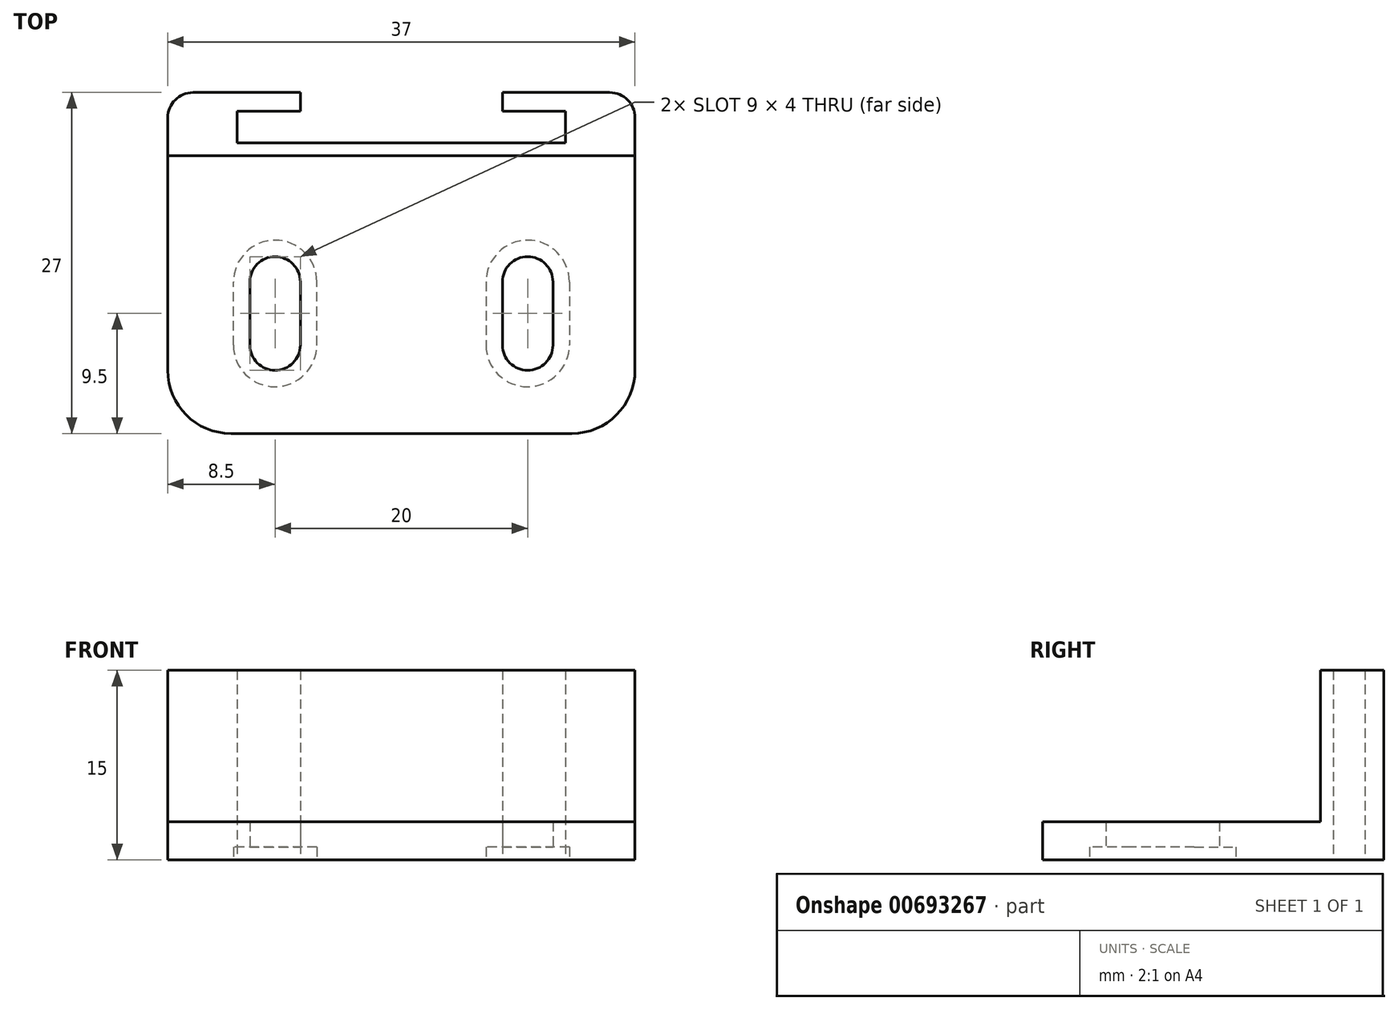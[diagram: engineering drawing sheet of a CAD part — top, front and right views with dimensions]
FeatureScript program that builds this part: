
annotation { "Feature Type Name" : "Feature", "Feature Type Description" : "" }
export const myFeature = defineFeature(function(context is Context, id is Id, definition is map)
    precondition{}
    {
        {
            var Q0;
            Q0=qCreatedBy(makeId("Top.planeOp"),FACE);
            var sketch = newSketch(context, id + "F0", { "sketchPlane" : qUnion([Q0])});
            skLineSegment(sketch, "E0.bottom", {"start": v(0, 0) * mm, "end": v(32, 0) * mm});
            skLineSegment(sketch, "E0.top", {"start": v(0, 22) * mm, "end": v(32, 22) * mm});
            skLineSegment(sketch, "E0.left", {"start": v(0, 0) * mm, "end": v(0, 22) * mm});
            skLineSegment(sketch, "E0.right", {"start": v(32, 0) * mm, "end": v(32, 22) * mm});
            skLineSegment(sketch, "E1.bottom", {"start": v(4, 5) * mm, "end": v(8, 5) * mm});
            skLineSegment(sketch, "E1.top", {"start": v(4, 14) * mm, "end": v(8, 14) * mm});
            skLineSegment(sketch, "E1.left", {"start": v(4, 5) * mm, "end": v(4, 14) * mm});
            skLineSegment(sketch, "E1.right", {"start": v(8, 5) * mm, "end": v(8, 14) * mm});
            skLineSegment(sketch, "E2.bottom", {"start": v(24, 14) * mm, "end": v(28, 14) * mm});
            skLineSegment(sketch, "E2.top", {"start": v(24, 5) * mm, "end": v(28, 5) * mm});
            skLineSegment(sketch, "E2.left", {"start": v(24, 14) * mm, "end": v(24, 5) * mm});
            skLineSegment(sketch, "E2.right", {"start": v(28, 14) * mm, "end": v(28, 5) * mm});
            skLineSegment(sketch, "E3", {"start": v(0, 22) * mm, "end": v(0, 23) * mm});
            skLineSegment(sketch, "E4", {"start": v(32, 22) * mm, "end": v(32, 23) * mm});
            skLineSegment(sketch, "E5", {"start": v(32, 23) * mm, "end": v(0, 23) * mm});
            skLineSegment(sketch, "E6", {"start": v(0, 23) * mm, "end": v(0, 27) * mm});
            skLineSegment(sketch, "E7", {"start": v(0, 27) * mm, "end": v(8, 27) * mm});
            skLineSegment(sketch, "E8", {"start": v(8, 27) * mm, "end": v(8, 25.5) * mm});
            skLineSegment(sketch, "E9", {"start": v(8, 25.5) * mm, "end": v(3, 25.5) * mm});
            skLineSegment(sketch, "E10", {"start": v(3, 25.5) * mm, "end": v(3, 23) * mm});
            skPoint(sketch, "E11", {"position": v(16, 23) * mm});
            skPoint(sketch, "E12", {"position": v(16, 0) * mm});
            skPoint(sketch, "E13", {"position": v(16, 22) * mm});
            skLineSegment(sketch, "E14", {"start": v(16, 23) * mm, "end": v(16, 0) * mm});
            skLineSegment(sketch, "E15.MirrorCS", {"start": v(32, 27) * mm, "end": v(24, 27) * mm});
            skLineSegment(sketch, "E16.MirrorCS", {"start": v(32, 23) * mm, "end": v(32, 27) * mm});
            skLineSegment(sketch, "E17.MirrorCS", {"start": v(29, 25.5) * mm, "end": v(29, 23) * mm});
            skLineSegment(sketch, "E18.MirrorCS", {"start": v(24, 25.5) * mm, "end": v(29, 25.5) * mm});
            skLineSegment(sketch, "E19.MirrorCS", {"start": v(24, 27) * mm, "end": v(24, 25.5) * mm});
            skSolve(sketch);
        }
        {
            var Q0;
            {var subQ0=sQuery(id+"F0.wireOp",EDGE,"E0.left");Q0=makeQuery(id+"F0.imprint","IMPRINT",FACE,{"disambiguationData":[TD([[makeQuery(id+"F0.imprint","IMPRINT",EDGE,{"derivedFrom":subQ0}),-1.0]])]});}
            var Q1;
            {var subQ0=sQuery(id+"F0.wireOp",EDGE,"E0.right");Q1=makeQuery(id+"F0.imprint","IMPRINT",FACE,{"disambiguationData":[TD([[makeQuery(id+"F0.imprint","IMPRINT",EDGE,{"derivedFrom":subQ0}),1.0]])]});}
            extrude(context, id + "F1", {"entities" : qUnion([Q0, Q1]), "depth" : 3 * mm, "offsetDistance" : 25 * mm});
        }
        {
            var Q0;
            {var subQ0=sQuery(id+"F0.wireOp",EDGE,"E6");Q0=makeQuery(id+"F0.imprint","IMPRINT",FACE,{"disambiguationData":[TD([[makeQuery(id+"F0.imprint","IMPRINT",EDGE,{"derivedFrom":subQ0}),-1.0]])]});}
            var Q1;
            {var subQ4=sQuery(id+"F0.wireOp",EDGE,"E3");Q1=makeQuery(id+"F0.imprint","IMPRINT",FACE,{"disambiguationData":[TD([[makeQuery(id+"F0.imprint","IMPRINT",EDGE,{"derivedFrom":subQ4}),-1.0]])]});}
            var Q2;
            {var subQ4=sQuery(id+"F0.wireOp",EDGE,"E4");Q2=makeQuery(id+"F0.imprint","IMPRINT",FACE,{"disambiguationData":[TD([[makeQuery(id+"F0.imprint","IMPRINT",EDGE,{"derivedFrom":subQ4}),1.0]])]});}
            var Q3;
            Q3=makeQuery(id+"F0.imprint","IMPRINT",FACE,{"disambiguationData":[TD([[makeQuery(id+"F0.imprint","IMPRINT",EDGE,{"derivedFrom":sQuery(id+"F0.wireOp",EDGE,"E15.MirrorCS")}),1.0]])]});
            extrude(context, id + "F2", {"entities" : qUnion([Q0, Q1, Q2, Q3]), "operationType" : NewBodyOperationType.ADD, "depth" : 15 * mm, "offsetDistance" : 25 * mm});
        }
        {
            var Q0;
            Q0=makeQuery(id+"F2.boolean.opBoolean","MERGE",FACE,{"derivedFrom":[makeQuery(id+"F1.opExtrude","SWEPT_FACE",FACE,{"disambiguationData":[OSD([sQuery(id+"F0.wireOp",EDGE,"E0.right")])]}),makeQuery(id+"F2.opExtrude","SWEPT_FACE",FACE,{"disambiguationData":[OSD([sQuery(id+"F0.wireOp",EDGE,"E4"),sQuery(id+"F0.wireOp",EDGE,"E16.MirrorCS")])]})]});
            extrude(context, id + "F3", {"entities" : qUnion([Q0]), "operationType" : NewBodyOperationType.ADD, "depth" : 2.5 * mm, "offsetDistance" : 25 * mm});
        }
        {
            var Q0;
            Q0=makeQuery(id+"F2.boolean.opBoolean","MERGE",FACE,{"derivedFrom":[makeQuery(id+"F1.opExtrude","SWEPT_FACE",FACE,{"disambiguationData":[OSD([sQuery(id+"F0.wireOp",EDGE,"E0.left")])]}),makeQuery(id+"F2.opExtrude","SWEPT_FACE",FACE,{"disambiguationData":[OSD([sQuery(id+"F0.wireOp",EDGE,"E3"),sQuery(id+"F0.wireOp",EDGE,"E6")])]})]});
            extrude(context, id + "F4", {"entities" : qUnion([Q0]), "operationType" : NewBodyOperationType.ADD, "depth" : 2.5 * mm, "offsetDistance" : 25 * mm});
        }
        {
            var Q0;
            Q0=makeQuery(id+"F2.opExtrude","SWEPT_EDGE",EDGE,{"disambiguationData":[OSD([sQuery(id+"F0.wireOp",EDGE,"E6"),sQuery(id+"F0.wireOp",EDGE,"E7")])]});
            var Q1;
            Q1=makeQuery(id+"F2.opExtrude","SWEPT_EDGE",EDGE,{"disambiguationData":[OSD([sQuery(id+"F0.wireOp",EDGE,"E15.MirrorCS"),sQuery(id+"F0.wireOp",EDGE,"E16.MirrorCS")])]});
            var Q2;
            Q2=makeQuery(id+"F3.opExtrude","CAP_EDGE",EDGE,{"disambiguationData":[OSD([sQuery(id+"F0.wireOp",EDGE,"E15.MirrorCS"),sQuery(id+"F0.wireOp",EDGE,"E16.MirrorCS")])],"isStart":false});
            var Q3;
            Q3=makeQuery(id+"F4.opExtrude","CAP_EDGE",EDGE,{"disambiguationData":[OSD([sQuery(id+"F0.wireOp",EDGE,"E6"),sQuery(id+"F0.wireOp",EDGE,"E7")])],"isStart":false});
            fillet(context, id + "F5", {"entities" : qUnion([Q0, Q1, Q2, Q3]), "radius" : 2 * mm, "tangentPropagation" : true, "allowEdgeOverflow" : false});
        }
        {
            var Q0;
            Q0=makeQuery(id+"F1.opExtrude","SWEPT_EDGE",EDGE,{"disambiguationData":[OSD([sQuery(id+"F0.wireOp",EDGE,"E2.bottom"),sQuery(id+"F0.wireOp",EDGE,"E2.left")])]});
            var Q1;
            Q1=makeQuery(id+"F1.opExtrude","SWEPT_EDGE",EDGE,{"disambiguationData":[OSD([sQuery(id+"F0.wireOp",EDGE,"E2.bottom"),sQuery(id+"F0.wireOp",EDGE,"E2.right")])]});
            var Q2;
            Q2=makeQuery(id+"F1.opExtrude","SWEPT_EDGE",EDGE,{"disambiguationData":[OSD([sQuery(id+"F0.wireOp",EDGE,"E1.top"),sQuery(id+"F0.wireOp",EDGE,"E1.right")])]});
            var Q3;
            Q3=makeQuery(id+"F1.opExtrude","SWEPT_EDGE",EDGE,{"disambiguationData":[OSD([sQuery(id+"F0.wireOp",EDGE,"E1.top"),sQuery(id+"F0.wireOp",EDGE,"E1.left")])]});
            var Q4;
            Q4=makeQuery(id+"F1.opExtrude","SWEPT_EDGE",EDGE,{"disambiguationData":[OSD([sQuery(id+"F0.wireOp",EDGE,"E2.top"),sQuery(id+"F0.wireOp",EDGE,"E2.right")])]});
            var Q5;
            Q5=makeQuery(id+"F1.opExtrude","SWEPT_EDGE",EDGE,{"disambiguationData":[OSD([sQuery(id+"F0.wireOp",EDGE,"E1.bottom"),sQuery(id+"F0.wireOp",EDGE,"E1.right")])]});
            var Q6;
            Q6=makeQuery(id+"F1.opExtrude","SWEPT_EDGE",EDGE,{"disambiguationData":[OSD([sQuery(id+"F0.wireOp",EDGE,"E1.bottom"),sQuery(id+"F0.wireOp",EDGE,"E1.left")])]});
            var Q7;
            Q7=makeQuery(id+"F1.opExtrude","SWEPT_EDGE",EDGE,{"disambiguationData":[OSD([sQuery(id+"F0.wireOp",EDGE,"E2.top"),sQuery(id+"F0.wireOp",EDGE,"E2.left")])]});
            fillet(context, id + "F6", {"entities" : qUnion([Q0, Q1, Q2, Q3, Q4, Q5, Q6, Q7]), "radius" : 2 * mm, "tangentPropagation" : true, "allowEdgeOverflow" : false});
        }
        {
            var Q0;
            {var subQ0=sQuery(id+"F0.wireOp",EDGE,"E0.left");Q0=makeQuery(id+"F0.imprint","IMPRINT",FACE,{"disambiguationData":[TD([[makeQuery(id+"F0.imprint","IMPRINT",EDGE,{"derivedFrom":subQ0}),-1.0]])]});}
            var sketch = newSketch(context, id + "F7", { "sketchPlane" : qUnion([Q0])});
            skArc(sketch, "E20.0", {"start": v(2.7, 7) * mm, "mid": v(6, 3.7) * mm, "end": v(9.3, 7) * mm});
            skLineSegment(sketch, "E21.0", {"start": v(2.7, 5) * mm, "end": v(2.7, 14) * mm});
            skLineSegment(sketch, "E22.0", {"start": v(9.3, 5) * mm, "end": v(9.3, 14) * mm});
            skArc(sketch, "E23.0", {"start": v(9.3, 12) * mm, "mid": v(6, 15.3) * mm, "end": v(2.7, 12) * mm});
            skSolve(sketch);
        }
        {
            var Q0;
            {var subQ2=sQuery(id+"F7.wireOp",EDGE,"E20.0");Q0=makeQuery(id+"F7.imprint","IMPRINT",FACE,{"disambiguationData":[TD([[makeQuery(id+"F7.imprint","IMPRINT",EDGE,{"derivedFrom":subQ2}),1.0]])]});}
            var Q1;
            Q1=makeQuery(id+"F7.imprint","IMPRINT",FACE,{"disambiguationData":[TD([[makeQuery(id+"F7.imprint","IMPRINT",EDGE,{"derivedFrom":makeQuery(id+"F0.imprint","IMPRINT",EDGE,{"derivedFrom":sQuery(id+"F0.wireOp",EDGE,"E1.bottom")})}),1.0]])]});
            extrude(context, id + "F8", {"entities" : qUnion([Q0, Q1]), "operationType" : NewBodyOperationType.REMOVE, "depth" : 1 * mm, "offsetDistance" : 25 * mm});
        }
        {
            var Q0;
            {var subQ0=sQuery(id+"F0.wireOp",EDGE,"E0.right");Q0=makeQuery(id+"F0.imprint","IMPRINT",FACE,{"disambiguationData":[TD([[makeQuery(id+"F0.imprint","IMPRINT",EDGE,{"derivedFrom":subQ0}),1.0]])]});}
            var sketch = newSketch(context, id + "F9", { "sketchPlane" : qUnion([Q0])});
            skArc(sketch, "E24.0", {"start": v(22.7, 7) * mm, "mid": v(26, 3.7) * mm, "end": v(29.3, 7) * mm});
            skArc(sketch, "E25.0", {"start": v(29.3, 12) * mm, "mid": v(26, 15.3) * mm, "end": v(22.7, 12) * mm});
            skLineSegment(sketch, "E26.0", {"start": v(22.7, 14) * mm, "end": v(22.7, 5) * mm});
            skLineSegment(sketch, "E27.0", {"start": v(29.3, 14) * mm, "end": v(29.3, 5) * mm});
            skSolve(sketch);
        }
        {
            var Q0;
            Q0 = qSketchRegion(id + "F9", true);
            extrude(context, id + "F10", {"entities" : qUnion([Q0]), "operationType" : NewBodyOperationType.REMOVE, "depth" : 1 * mm, "offsetDistance" : 25 * mm});
        }
        {
            var Q0;
            Q0=makeQuery(id+"F1.opExtrude","SWEPT_EDGE",EDGE,{"disambiguationData":[OSD([sQuery(id+"F0.wireOp",EDGE,"E0.bottom"),sQuery(id+"F0.wireOp",EDGE,"E0.right")])]});
            var Q1;
            Q1=makeQuery(id+"F1.opExtrude","SWEPT_EDGE",EDGE,{"disambiguationData":[OSD([sQuery(id+"F0.wireOp",EDGE,"E0.bottom"),sQuery(id+"F0.wireOp",EDGE,"E0.left")])]});
            var Q2;
            Q2=makeQuery(id+"F3.opExtrude","CAP_EDGE",EDGE,{"disambiguationData":[OSD([sQuery(id+"F0.wireOp",EDGE,"E0.bottom"),sQuery(id+"F0.wireOp",EDGE,"E0.right")])],"isStart":false});
            var Q3;
            Q3=makeQuery(id+"F4.opExtrude","CAP_EDGE",EDGE,{"disambiguationData":[OSD([sQuery(id+"F0.wireOp",EDGE,"E0.bottom"),sQuery(id+"F0.wireOp",EDGE,"E0.left")])],"isStart":false});
            fillet(context, id + "F11", {"entities" : qUnion([Q0, Q1, Q2, Q3]), "radius" : 5 * mm, "tangentPropagation" : true, "allowEdgeOverflow" : false});
        }
    });
